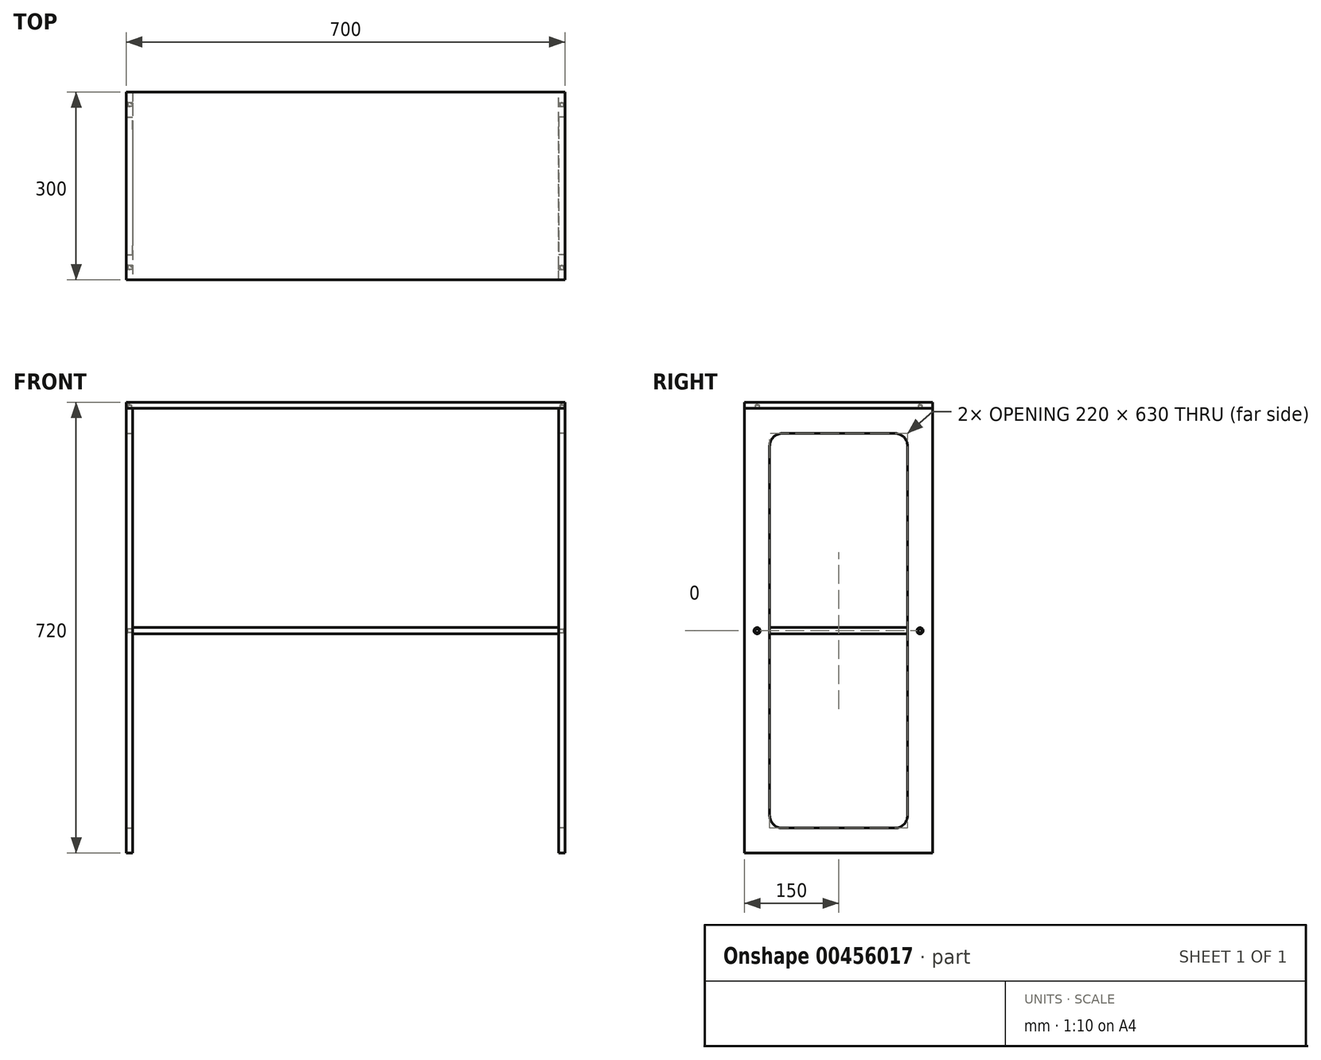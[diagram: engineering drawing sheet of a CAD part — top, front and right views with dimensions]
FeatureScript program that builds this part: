
annotation { "Feature Type Name" : "Feature", "Feature Type Description" : "" }
export const myFeature = defineFeature(function(context is Context, id is Id, definition is map)
    precondition{}
    {
        {
            assignVariable(context, id + "F0", {"name" : "epaisseur", "anyValue" : 10});
        }
        {
            assignVariable(context, id + "F1", {"name" : "largeur", "anyValue" : 700});
        }
        {
            var Q0;
            Q0=qCreatedBy(makeId("Right.planeOp"),FACE);
            cPlane(context, id + "F2", {"entities" : qUnion([Q0]), "cplaneType" : CPlaneType.OFFSET, "offset" : (getVariable(context, 'largeur') / 2 - getVariable(context, 'epaisseur')) * mm, "width" : 150 * mm, "height" : 150 * mm});
        }
        {
            var Q0;
            Q0=qCreatedBy(id+"F2.planeOp",FACE);
            var sketch = newSketch(context, id + "F3", { "sketchPlane" : qUnion([Q0])});
            skLineSegment(sketch, "E0.bottom", {"start": v(150, -355) * mm, "end": v(-150, -355) * mm});
            skLineSegment(sketch, "E0.top", {"start": v(150, 355) * mm, "end": v(-150, 355) * mm});
            skLineSegment(sketch, "E0.left", {"start": v(150, -355) * mm, "end": v(150, 355) * mm});
            skLineSegment(sketch, "E0.right", {"start": v(-150, -355) * mm, "end": v(-150, 355) * mm});
            skPoint(sketch, "E0.middle", {"position": v(0, 0) * mm});
            skLineSegment(sketch, "E1", {"start": v(-150, -5) * mm, "end": v(150, -5) * mm});
            skLineSegment(sketch, "E2.0", {"start": v(110, 315) * mm, "end": v(-110, 315) * mm});
            skLineSegment(sketch, "E2.1", {"start": v(110, -315) * mm, "end": v(110, 315) * mm});
            skLineSegment(sketch, "E2.2", {"start": v(110, -315) * mm, "end": v(-110, -315) * mm});
            skLineSegment(sketch, "E2.3", {"start": v(-110, -315) * mm, "end": v(-110, 315) * mm});
            skPoint(sketch, "E3", {"position": v(-130, 0) * mm});
            skPoint(sketch, "E4", {"position": v(130, 0) * mm});
            skSolve(sketch);
        }
        {
            var Q0;
            {var subQ5=sQuery(id+"F3.wireOp",EDGE,"E0.bottom");Q0=makeQuery(id+"F3.imprint","IMPRINT",FACE,{"disambiguationData":[TD([[makeQuery(id+"F3.imprint","IMPRINT",EDGE,{"derivedFrom":subQ5}),-1.0]])]});}
            var Q1;
            {var subQ1=sQuery(id+"F3.wireOp",EDGE,"E0.top");Q1=makeQuery(id+"F3.imprint","IMPRINT",FACE,{"disambiguationData":[TD([[makeQuery(id+"F3.imprint","IMPRINT",EDGE,{"derivedFrom":subQ1}),1.0]])]});}
            extrude(context, id + "F4", {"entities" : qUnion([Q0, Q1]), "depth" : (getVariable(context, 'epaisseur')) * mm});
        }
        {
            var Q0;
            Q0=makeQuery(id+"F4.opExtrude","CAP_FACE",FACE,{"disambiguationData":[OSD([sQuery(id+"F3.wireOp",EDGE,"E0.bottom"),sQuery(id+"F3.wireOp",EDGE,"E0.top"),sQuery(id+"F3.wireOp",EDGE,"E0.left"),sQuery(id+"F3.wireOp",EDGE,"E0.right"),sQuery(id+"F3.wireOp",EDGE,"E2.0"),sQuery(id+"F3.wireOp",EDGE,"E2.1"),sQuery(id+"F3.wireOp",EDGE,"E2.2"),sQuery(id+"F3.wireOp",EDGE,"E2.3")])],"isStart":false});
            var sketch = newSketch(context, id + "F5", { "sketchPlane" : qUnion([Q0])});
            skPoint(sketch, "E5.0", {"position": v(-130, 0) * mm});
            skPoint(sketch, "E5.1", {"position": v(130, 0) * mm});
            skSolve(sketch);
        }
        {
            var Q0;
            Q0=sQuery(id+"F5.wireOp",VERTEX,"E5.0");
            var Q1;
            Q1=sQuery(id+"F5.wireOp",VERTEX,"E5.1");
            var Q2;
            Q2=makeQuery(id+"F4.opExtrude","SWEPT_BODY",BODY,{"disambiguationData":[OSD([sQuery(id+"F3.wireOp",EDGE,"E0.bottom"),sQuery(id+"F3.wireOp",EDGE,"E0.top"),sQuery(id+"F3.wireOp",EDGE,"E0.left"),sQuery(id+"F3.wireOp",EDGE,"E0.right"),sQuery(id+"F3.wireOp",EDGE,"E2.0"),sQuery(id+"F3.wireOp",EDGE,"E2.1"),sQuery(id+"F3.wireOp",EDGE,"E2.2"),sQuery(id+"F3.wireOp",EDGE,"E2.3")])]});
            hole(context, id + "F6", {"style" : HoleStyle.C_SINK, "endStyle" : HoleEndStyle.THROUGH, "holeDiameter" : 6 * mm, "cSinkDiameter" : 10 * mm, "cSinkAngle" : 90 * degree, "majorDiameter" : 5 * mm, "isTappedThrough" : true, "tappedDepth" : 12 * mm, "tapClearance" : 3, "locations" : qUnion([Q0, Q1]), "scope" : qUnion([Q2])});
        }
        {
            var Q0;
            Q0=makeQuery(id+"F4.opExtrude","CAP_EDGE",EDGE,{"disambiguationData":[OSD([sQuery(id+"F3.wireOp",EDGE,"E0.top")])],"isStart":true});
            cPoint(context, id + "F7", {"entities" : qUnion([Q0]), "parameter" : 0.5});
        }
        {
            var Q0;
            Q0=qCreatedBy(makeId("Top.planeOp"),FACE);
            var Q1;
            Q1 = qCreatedBy(id + "F7" ,VERTEX);
            cPlane(context, id + "F8", {"entities" : qUnion([Q0, Q1]), "cplaneType" : CPlaneType.PLANE_POINT, "offset" : 25 * mm, "width" : 150 * mm, "height" : 150 * mm});
        }
        {
            var Q0;
            Q0=qCreatedBy(id+"F8.planeOp",FACE);
            var sketch = newSketch(context, id + "F9", { "sketchPlane" : qUnion([Q0])});
            skLineSegment(sketch, "E6.bottom", {"start": v(350, -150) * mm, "end": v(-350, -150) * mm});
            skLineSegment(sketch, "E6.top", {"start": v(350, 150) * mm, "end": v(-350, 150) * mm});
            skLineSegment(sketch, "E6.left", {"start": v(350, -150) * mm, "end": v(350, 150) * mm});
            skLineSegment(sketch, "E6.right", {"start": v(-350, -150) * mm, "end": v(-350, 150) * mm});
            skPoint(sketch, "E6.middle", {"position": v(0, 0) * mm});
            skPoint(sketch, "E7", {"position": v(345, 130) * mm});
            skPoint(sketch, "E8", {"position": v(345, -130) * mm});
            skLineSegment(sketch, "E9", {"start": v(0, -150) * mm, "end": v(0, 150) * mm, "construction": true});
            skPoint(sketch, "E10.MirrorP", {"position": v(-345, 130) * mm});
            skPoint(sketch, "E11.MirrorP", {"position": v(-345, -130) * mm});
            skSolve(sketch);
        }
        {
            var Q0;
            Q0=makeQuery(id+"F9.imprint","IMPRINT",FACE,{"disambiguationData":[TD([[makeQuery(id+"F9.imprint","IMPRINT",EDGE,{"derivedFrom":sQuery(id+"F9.wireOp",EDGE,"E6.bottom")}),-1.0]])]});
            extrude(context, id + "F10", {"entities" : qUnion([Q0]), "depth" : (getVariable(context, 'epaisseur')) * mm, "offsetDistance" : 25 * mm});
        }
        {
            var Q0;
            Q0=sQuery(id+"F9.wireOp",VERTEX,"E11.MirrorP");
            var Q1;
            Q1=sQuery(id+"F9.wireOp",VERTEX,"E10.MirrorP");
            var Q2;
            Q2=sQuery(id+"F9.wireOp",VERTEX,"E8");
            var Q3;
            Q3=sQuery(id+"F9.wireOp",VERTEX,"E7");
            var Q4;
            Q4=makeQuery(id+"F10.opExtrude","SWEPT_BODY",BODY,{"disambiguationData":[OSD([sQuery(id+"F9.wireOp",EDGE,"E6.bottom"),sQuery(id+"F9.wireOp",EDGE,"E6.top"),sQuery(id+"F9.wireOp",EDGE,"E6.left"),sQuery(id+"F9.wireOp",EDGE,"E6.right")])]});
            hole(context, id + "F11", {"style" : HoleStyle.SIMPLE, "endStyle" : HoleEndStyle.BLIND, "oppositeDirection" : true, "holeDiameter" : 6 * mm, "majorDiameter" : 5 * mm, "holeDepth" : (getVariable(context, 'epaisseur') / 2) * mm, "isTappedThrough" : true, "tappedDepth" : 12 * mm, "tapClearance" : 3, "locations" : qUnion([Q0, Q1, Q2, Q3]), "scope" : qUnion([Q4])});
        }
        {
            var Q0;
            Q0=qCreatedBy(makeId("Top.planeOp"),FACE);
            var sketch = newSketch(context, id + "F12", { "sketchPlane" : qUnion([Q0])});
            skLineSegment(sketch, "E12.bottom", {"start": v(340, -150) * mm, "end": v(-340, -150) * mm});
            skLineSegment(sketch, "E12.top", {"start": v(340, 150) * mm, "end": v(-340, 150) * mm});
            skLineSegment(sketch, "E12.left", {"start": v(340, -150) * mm, "end": v(340, 150) * mm});
            skLineSegment(sketch, "E12.right", {"start": v(-340, -150) * mm, "end": v(-340, 150) * mm});
            skPoint(sketch, "E12.middle", {"position": v(0, 0) * mm});
            skSolve(sketch);
        }
        {
            var Q0;
            Q0=makeQuery(id+"F12.imprint","IMPRINT",FACE,{"disambiguationData":[TD([[makeQuery(id+"F12.imprint","IMPRINT",EDGE,{"derivedFrom":sQuery(id+"F12.wireOp",EDGE,"E12.bottom")}),-1.0]])]});
            extrude(context, id + "F13", {"entities" : qUnion([Q0]), "depth" : (getVariable(context, 'epaisseur') / 2) * mm, "hasSecondDirection" : true, "secondDirectionOppositeDirection" : true, "secondDirectionDepth" : (getVariable(context, 'epaisseur') / 2) * mm, "offsetDistance" : 25 * mm});
        }
        {
            var Q0;
            Q0=makeQuery(id+"F4.opExtrude","SWEPT_EDGE",EDGE,{"disambiguationData":[OSD([sQuery(id+"F3.wireOp",EDGE,"E2.0"),sQuery(id+"F3.wireOp",EDGE,"E2.3")])]});
            var Q1;
            Q1=makeQuery(id+"F4.opExtrude","SWEPT_EDGE",EDGE,{"disambiguationData":[OSD([sQuery(id+"F3.wireOp",EDGE,"E2.0"),sQuery(id+"F3.wireOp",EDGE,"E2.1")])]});
            var Q2;
            Q2=makeQuery(id+"F4.opExtrude","SWEPT_EDGE",EDGE,{"disambiguationData":[OSD([sQuery(id+"F3.wireOp",EDGE,"E2.1"),sQuery(id+"F3.wireOp",EDGE,"E2.2")])]});
            var Q3;
            Q3=makeQuery(id+"F4.opExtrude","SWEPT_EDGE",EDGE,{"disambiguationData":[OSD([sQuery(id+"F3.wireOp",EDGE,"E2.2"),sQuery(id+"F3.wireOp",EDGE,"E2.3")])]});
            fillet(context, id + "F14", {"entities" : qUnion([Q0, Q1, Q2, Q3]), "radius" : (2 * getVariable(context, 'epaisseur')) * mm, "tangentPropagation" : true, "allowEdgeOverflow" : false});
        }
        {
            var Q0;
            Q0=makeQuery(id+"F4.opExtrude","SWEPT_BODY",BODY,{"disambiguationData":[OSD([sQuery(id+"F3.wireOp",EDGE,"E0.bottom"),sQuery(id+"F3.wireOp",EDGE,"E0.top"),sQuery(id+"F3.wireOp",EDGE,"E0.left"),sQuery(id+"F3.wireOp",EDGE,"E0.right"),sQuery(id+"F3.wireOp",EDGE,"E2.0"),sQuery(id+"F3.wireOp",EDGE,"E2.1"),sQuery(id+"F3.wireOp",EDGE,"E2.2"),sQuery(id+"F3.wireOp",EDGE,"E2.3"),sQuery(id+"F3.wireOp",EDGE,"i5ZDcfM3-Roj8-fqVX-Hq5e-uanwNH8U28TX"),sQuery(id+"F3.wireOp",EDGE,"dSUf0mVc-5Txp-OUE6-imvN-OMBtca615pVX")])]});
            var Q1;
            Q1=qCreatedBy(makeId("Right.planeOp"),FACE);
            mirror(context, id + "F15", {"entities" : qUnion([Q0]), "mirrorPlane" : qUnion([Q1])});
        }
    });
